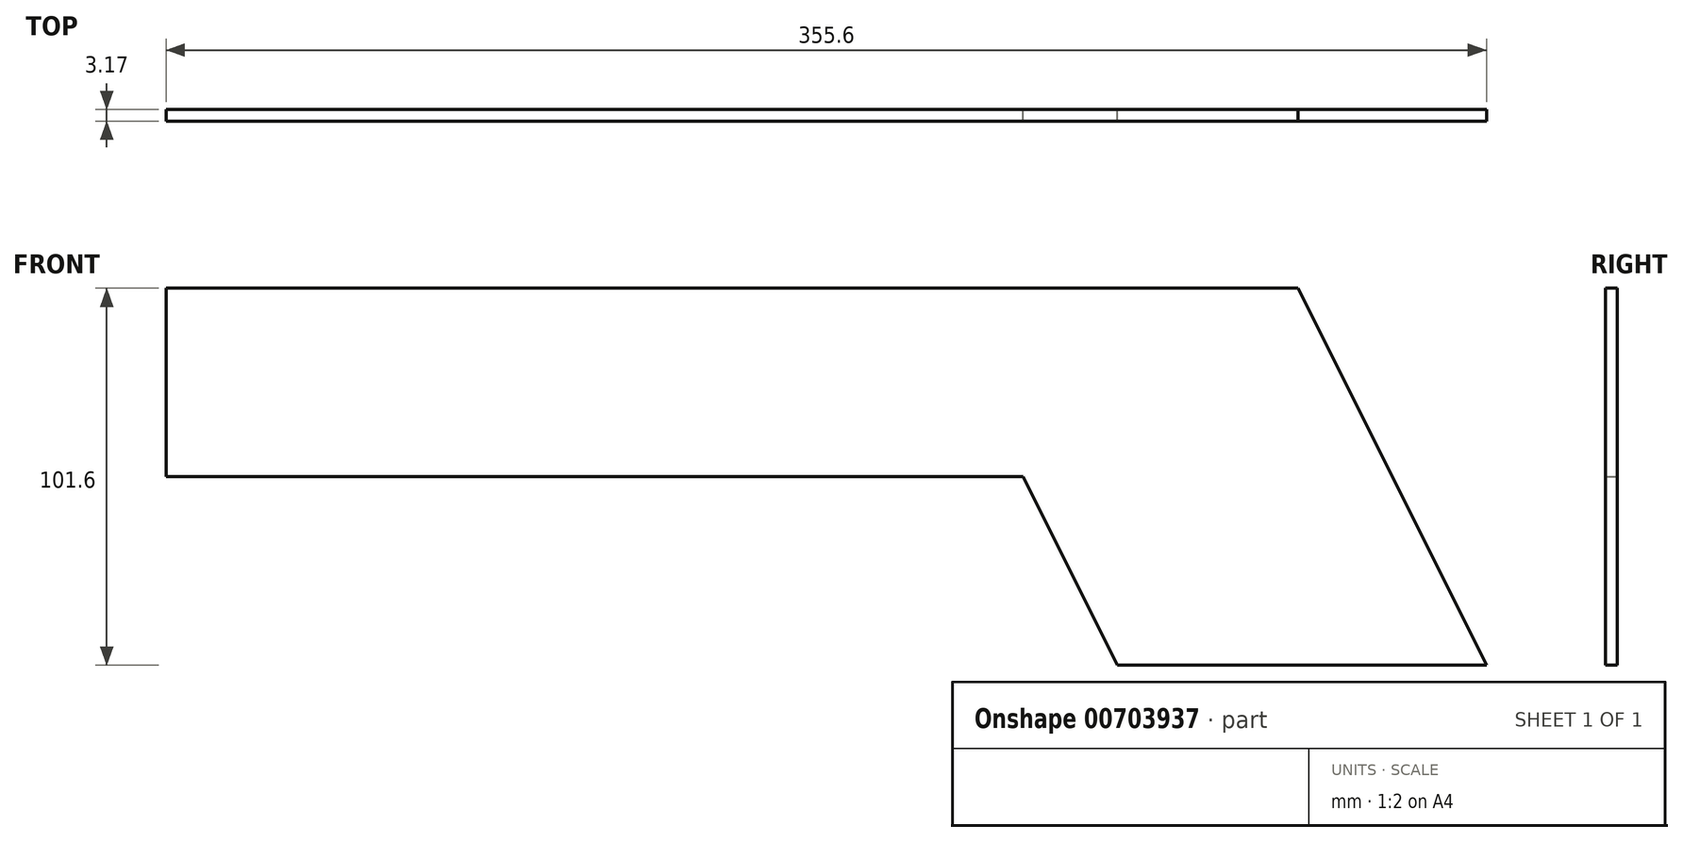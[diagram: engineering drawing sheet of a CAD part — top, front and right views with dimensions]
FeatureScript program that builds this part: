
annotation { "Feature Type Name" : "Feature", "Feature Type Description" : "" }
export const myFeature = defineFeature(function(context is Context, id is Id, definition is map)
    precondition{}
    {
        {
            var Q0;
            Q0=qCreatedBy(makeId("Front.planeOp"),FACE);
            var sketch = newSketch(context, id + "F0", { "sketchPlane" : qUnion([Q0])});
            skLineSegment(sketch, "E0", {"start": v(0, 0) * mm, "end": v(0, -50.8) * mm});
            skLineSegment(sketch, "E1", {"start": v(-256.2, -101.6) * mm, "end": v(-355.6, -101.6) * mm});
            skLineSegment(sketch, "E2", {"start": v(-355.6, -101.6) * mm, "end": v(-256.2, -101.6) * mm});
            skLineSegment(sketch, "E3", {"start": v(-304.8, 0) * mm, "end": v(-355.6, -101.6) * mm});
            skLineSegment(sketch, "E4", {"start": v(304.8, 0) * mm, "end": v(355.6, -101.6) * mm});
            skLineSegment(sketch, "E5", {"start": v(406.4, 304.8) * mm, "end": v(304.8, 0) * mm});
            skLineSegment(sketch, "E6", {"start": v(-389.47, 254) * mm, "end": v(-406.4, 304.8) * mm});
            skLineSegment(sketch, "E7", {"start": v(-318.99, 203.2) * mm, "end": v(-306.29, 165.1) * mm});
            skLineSegment(sketch, "E8", {"start": v(-166.59, 50.8) * mm, "end": v(268.19, 50.8) * mm});
            skLineSegment(sketch, "E9", {"start": v(335.92, 254) * mm, "end": v(-335.92, 254) * mm});
            skLineSegment(sketch, "E10", {"start": v(335.92, 254) * mm, "end": v(268.19, 50.8) * mm});
            skLineSegment(sketch, "E11", {"start": v(-256.2, -101.6) * mm, "end": v(-230.8, -50.8) * mm});
            skLineSegment(sketch, "E12", {"start": v(-230.8, -50.8) * mm, "end": v(230.8, -50.8) * mm});
            skLineSegment(sketch, "E13", {"start": v(230.8, -50.8) * mm, "end": v(256.2, -101.6) * mm});
            skLineSegment(sketch, "E14.trimOffspring", {"start": v(256.2, -101.6) * mm, "end": v(355.6, -101.6) * mm});
            skPoint(sketch, "E15.orphan", {"position": v(0, -101.6) * mm});
            skPoint(sketch, "E16", {"position": v(-215.9, 0) * mm});
            skPoint(sketch, "E17", {"position": v(-88.9, 0) * mm});
            skPoint(sketch, "E18", {"position": v(88.9, 0) * mm});
            skPoint(sketch, "E19", {"position": v(215.9, 0) * mm});
            skLineSegment(sketch, "E20", {"start": v(-217.39, 50.8) * mm, "end": v(-242.79, 76.2) * mm});
            skPoint(sketch, "E21.end.orphan", {"position": v(-391.2, 0) * mm});
            skLineSegment(sketch, "E22.1.0.0", {"start": v(-191.99, 76.2) * mm, "end": v(-217.39, 101.6) * mm});
            skLineSegment(sketch, "E22.2.0.0", {"start": v(-115.79, 50.8) * mm, "end": v(-141.19, 76.2) * mm});
            skLineSegment(sketch, "E22.3.0.0", {"start": v(-90.39, 76.2) * mm, "end": v(-115.79, 101.6) * mm});
            skLineSegment(sketch, "E22.4.0.0", {"start": v(-14.19, 50.8) * mm, "end": v(-39.59, 76.2) * mm});
            skLineSegment(sketch, "E22.5.0.0", {"start": v(11.21, 76.2) * mm, "end": v(-14.19, 101.6) * mm});
            skLineSegment(sketch, "E22.6.0.0", {"start": v(87.41, 50.8) * mm, "end": v(62.01, 76.2) * mm});
            skLineSegment(sketch, "E22.7.0.0", {"start": v(112.81, 76.2) * mm, "end": v(87.41, 101.6) * mm});
            skLineSegment(sketch, "E22.8.0.0", {"start": v(189.01, 50.8) * mm, "end": v(163.61, 76.2) * mm});
            skLineSegment(sketch, "E22.9.0.0", {"start": v(214.41, 76.2) * mm, "end": v(189.01, 101.6) * mm});
            skLineSegment(sketch, "E22.10.0.0", {"start": v(273.8, 67.62) * mm, "end": v(265.21, 76.2) * mm});
            skLineSegment(sketch, "E22.12.0.0", {"start": v(290.61, 152.4) * mm, "end": v(265.21, 177.8) * mm});
            skLineSegment(sketch, "E22.14.0.0", {"start": v(324.6, 220.02) * mm, "end": v(316.01, 228.6) * mm});
            skLineSegment(sketch, "E22.direction1", {"start": v(-420.59, 254) * mm, "end": v(-369.79, 254) * mm, "construction": true});
            skLineSegment(sketch, "E23.3.0.0", {"start": v(-166.59, 254) * mm, "end": v(-191.99, 228.6) * mm});
            skLineSegment(sketch, "E23.4.0.0", {"start": v(-141.19, 228.6) * mm, "end": v(-166.59, 203.2) * mm});
            skLineSegment(sketch, "E23.5.0.0", {"start": v(-64.99, 254) * mm, "end": v(-90.39, 228.6) * mm});
            skLineSegment(sketch, "E23.6.0.0", {"start": v(-39.59, 228.6) * mm, "end": v(-64.99, 203.2) * mm});
            skLineSegment(sketch, "E23.7.0.0", {"start": v(36.61, 254) * mm, "end": v(11.21, 228.6) * mm});
            skLineSegment(sketch, "E23.8.0.0", {"start": v(62.01, 228.6) * mm, "end": v(36.61, 203.2) * mm});
            skLineSegment(sketch, "E23.9.0.0", {"start": v(138.21, 254) * mm, "end": v(112.81, 228.6) * mm});
            skLineSegment(sketch, "E23.10.0.0", {"start": v(163.61, 228.6) * mm, "end": v(138.21, 203.2) * mm});
            skLineSegment(sketch, "E23.11.0.0", {"start": v(239.81, 254) * mm, "end": v(214.41, 228.6) * mm});
            skLineSegment(sketch, "E23.12.0.0", {"start": v(265.21, 228.6) * mm, "end": v(239.81, 203.2) * mm});
            skLineSegment(sketch, "E23.13.0.0", {"start": v(333.17, 245.76) * mm, "end": v(316.01, 228.6) * mm});
            skPoint(sketch, "E24.orphan", {"position": v(-420.59, 50.8) * mm});
            skPoint(sketch, "E25.orphan", {"position": v(-369.79, 50.8) * mm});
            skPoint(sketch, "E26.orphan", {"position": v(-318.99, 50.8) * mm});
            skPoint(sketch, "E27.orphan", {"position": v(290.61, 50.8) * mm});
            skLineSegment(sketch, "E28.trimOffspring", {"start": v(265.21, 127) * mm, "end": v(239.81, 152.4) * mm});
            skPoint(sketch, "E29.orphan", {"position": v(392.21, 50.8) * mm});
            skLineSegment(sketch, "E30.trimOffspring", {"start": v(311.9, 181.92) * mm, "end": v(290.61, 203.2) * mm});
            skPoint(sketch, "E31.orphan", {"position": v(493.81, 50.8) * mm});
            skLineSegment(sketch, "E32.trimOffspring", {"start": v(307.77, 169.56) * mm, "end": v(290.61, 152.4) * mm});
            skPoint(sketch, "E33.orphan", {"position": v(341.41, 254) * mm});
            skPoint(sketch, "E23.direction1.start.orphan", {"position": v(-522.19, 50.8) * mm});
            skLineSegment(sketch, "E34.trimOffspring", {"start": v(-268.19, 203.2) * mm, "end": v(-293.59, 228.6) * mm});
            skLineSegment(sketch, "E35.trimOffspring", {"start": v(-293.59, 177.8) * mm, "end": v(-318.99, 203.2) * mm});
            skLineSegment(sketch, "E36.trimOffspring", {"start": v(-268.19, 152.4) * mm, "end": v(-293.59, 127) * mm});
            skLineSegment(sketch, "E37.trimOffspring", {"start": v(-217.39, 203.2) * mm, "end": v(-242.79, 177.8) * mm});
            skLineSegment(sketch, "E38.trimOffspring", {"start": v(-242.79, 127) * mm, "end": v(-268.19, 101.6) * mm});
            skLineSegment(sketch, "E39.trimOffspring", {"start": v(-268.19, 101.6) * mm, "end": v(-293.59, 127) * mm});
            skLineSegment(sketch, "E40.trimOffspring", {"start": v(-242.79, 127) * mm, "end": v(-268.19, 152.4) * mm});
            skPoint(sketch, "E41.orphan", {"position": v(-166.59, 50.8) * mm});
            skLineSegment(sketch, "E42.trimOffspring", {"start": v(-166.59, 101.6) * mm, "end": v(-191.99, 127) * mm});
            skLineSegment(sketch, "E43.trimOffspring", {"start": v(-217.39, 152.4) * mm, "end": v(-242.79, 177.8) * mm});
            skLineSegment(sketch, "E44.trimOffspring", {"start": v(-191.99, 76.2) * mm, "end": v(-217.39, 50.8) * mm});
            skLineSegment(sketch, "E45.trimOffspring", {"start": v(-141.19, 127) * mm, "end": v(-166.59, 152.4) * mm});
            skLineSegment(sketch, "E46.trimOffspring", {"start": v(-166.59, 152.4) * mm, "end": v(-191.99, 127) * mm});
            skLineSegment(sketch, "E47.trimOffspring", {"start": v(-191.99, 177.8) * mm, "end": v(-217.39, 203.2) * mm});
            skLineSegment(sketch, "E48.trimOffspring", {"start": v(-191.99, 177.8) * mm, "end": v(-217.39, 152.4) * mm});
            skLineSegment(sketch, "E49.trimOffspring", {"start": v(-242.79, 228.6) * mm, "end": v(-268.19, 254) * mm});
            skPoint(sketch, "E50.orphan", {"position": v(-217.39, 254) * mm});
            skLineSegment(sketch, "E51.trimOffspring", {"start": v(-166.59, 203.2) * mm, "end": v(-191.99, 228.6) * mm});
            skLineSegment(sketch, "E52.trimOffspring", {"start": v(-141.19, 228.6) * mm, "end": v(-166.59, 254) * mm});
            skLineSegment(sketch, "E53.trimOffspring", {"start": v(-115.79, 203.2) * mm, "end": v(-141.19, 177.8) * mm});
            skLineSegment(sketch, "E54.trimOffspring", {"start": v(-90.39, 177.8) * mm, "end": v(-115.79, 152.4) * mm});
            skLineSegment(sketch, "E55.trimOffspring", {"start": v(-90.39, 177.8) * mm, "end": v(-115.79, 203.2) * mm});
            skLineSegment(sketch, "E56.trimOffspring", {"start": v(-115.79, 152.4) * mm, "end": v(-141.19, 177.8) * mm});
            skLineSegment(sketch, "E57.trimOffspring", {"start": v(-115.79, 101.6) * mm, "end": v(-141.19, 76.2) * mm});
            skLineSegment(sketch, "E58.trimOffspring", {"start": v(-90.39, 76.2) * mm, "end": v(-115.79, 50.8) * mm});
            skPoint(sketch, "E59.orphan", {"position": v(-64.99, 50.8) * mm});
            skLineSegment(sketch, "E60.trimOffspring", {"start": v(-64.99, 101.6) * mm, "end": v(-90.39, 127) * mm});
            skLineSegment(sketch, "E61.trimOffspring", {"start": v(-39.59, 127) * mm, "end": v(-64.99, 152.4) * mm});
            skLineSegment(sketch, "E62.trimOffspring", {"start": v(-39.59, 127) * mm, "end": v(-64.99, 101.6) * mm});
            skLineSegment(sketch, "E63.trimOffspring", {"start": v(-64.99, 152.4) * mm, "end": v(-90.39, 127) * mm});
            skPoint(sketch, "E64.orphan", {"position": v(-115.79, 254) * mm});
            skLineSegment(sketch, "E65.trimOffspring", {"start": v(-64.99, 203.2) * mm, "end": v(-90.39, 228.6) * mm});
            skLineSegment(sketch, "E66.trimOffspring", {"start": v(-39.59, 228.6) * mm, "end": v(-64.99, 254) * mm});
            skLineSegment(sketch, "E67.trimOffspring", {"start": v(-14.19, 101.6) * mm, "end": v(-39.59, 76.2) * mm});
            skLineSegment(sketch, "E68.trimOffspring", {"start": v(-14.19, 203.2) * mm, "end": v(-39.59, 177.8) * mm});
            skLineSegment(sketch, "E69.trimOffspring", {"start": v(11.21, 177.8) * mm, "end": v(-14.19, 152.4) * mm});
            skLineSegment(sketch, "E70.trimOffspring", {"start": v(11.21, 177.8) * mm, "end": v(-14.19, 203.2) * mm});
            skLineSegment(sketch, "E71.trimOffspring", {"start": v(-14.19, 152.4) * mm, "end": v(-39.59, 177.8) * mm});
            skLineSegment(sketch, "E72.trimOffspring", {"start": v(11.21, 76.2) * mm, "end": v(-14.19, 50.8) * mm});
            skPoint(sketch, "E73.orphan", {"position": v(36.61, 50.8) * mm});
            skLineSegment(sketch, "E74.trimOffspring", {"start": v(36.61, 101.6) * mm, "end": v(11.21, 127) * mm});
            skPoint(sketch, "E75.orphan", {"position": v(-14.19, 254) * mm});
            skLineSegment(sketch, "E76.trimOffspring", {"start": v(36.61, 203.2) * mm, "end": v(11.21, 228.6) * mm});
            skLineSegment(sketch, "E77.trimOffspring", {"start": v(62.01, 228.6) * mm, "end": v(36.61, 254) * mm});
            skLineSegment(sketch, "E78.trimOffspring", {"start": v(36.61, 152.4) * mm, "end": v(11.21, 127) * mm});
            skPoint(sketch, "E79.orphan", {"position": v(87.41, 254) * mm});
            skLineSegment(sketch, "E80.trimOffspring", {"start": v(62.01, 127) * mm, "end": v(36.61, 101.6) * mm});
            skLineSegment(sketch, "E81.trimOffspring", {"start": v(112.81, 177.8) * mm, "end": v(87.41, 152.4) * mm});
            skLineSegment(sketch, "E82.trimOffspring", {"start": v(87.41, 203.2) * mm, "end": v(62.01, 177.8) * mm});
            skLineSegment(sketch, "E83.trimOffspring", {"start": v(62.01, 127) * mm, "end": v(36.61, 152.4) * mm});
            skLineSegment(sketch, "E84.trimOffspring", {"start": v(87.41, 101.6) * mm, "end": v(62.01, 76.2) * mm});
            skLineSegment(sketch, "E85.trimOffspring", {"start": v(87.41, 152.4) * mm, "end": v(62.01, 177.8) * mm});
            skLineSegment(sketch, "E86.trimOffspring", {"start": v(112.81, 177.8) * mm, "end": v(87.41, 203.2) * mm});
            skPoint(sketch, "E87.orphan", {"position": v(138.21, 50.8) * mm});
            skLineSegment(sketch, "E88.trimOffspring", {"start": v(112.81, 76.2) * mm, "end": v(87.41, 50.8) * mm});
            skLineSegment(sketch, "E89.trimOffspring", {"start": v(138.21, 101.6) * mm, "end": v(112.81, 127) * mm});
            skLineSegment(sketch, "E90.trimOffspring", {"start": v(163.61, 127) * mm, "end": v(138.21, 152.4) * mm});
            skLineSegment(sketch, "E91.trimOffspring", {"start": v(138.21, 152.4) * mm, "end": v(112.81, 127) * mm});
            skLineSegment(sketch, "E92.trimOffspring", {"start": v(163.61, 127) * mm, "end": v(138.21, 101.6) * mm});
            skLineSegment(sketch, "E93.trimOffspring", {"start": v(189.01, 101.6) * mm, "end": v(163.61, 76.2) * mm});
            skLineSegment(sketch, "E94.trimOffspring", {"start": v(138.21, 203.2) * mm, "end": v(112.81, 228.6) * mm});
            skLineSegment(sketch, "E95.trimOffspring", {"start": v(163.61, 228.6) * mm, "end": v(138.21, 254) * mm});
            skLineSegment(sketch, "E96.trimOffspring", {"start": v(189.01, 203.2) * mm, "end": v(163.61, 177.8) * mm});
            skLineSegment(sketch, "E97.trimOffspring", {"start": v(214.41, 177.8) * mm, "end": v(189.01, 152.4) * mm});
            skLineSegment(sketch, "E98.trimOffspring", {"start": v(214.41, 177.8) * mm, "end": v(189.01, 203.2) * mm});
            skLineSegment(sketch, "E99.trimOffspring", {"start": v(189.01, 152.4) * mm, "end": v(163.61, 177.8) * mm});
            skLineSegment(sketch, "E100.trimOffspring", {"start": v(214.41, 76.2) * mm, "end": v(189.01, 50.8) * mm});
            skPoint(sketch, "E101.orphan", {"position": v(239.81, 50.8) * mm});
            skPoint(sketch, "E102.orphan", {"position": v(189.01, 254) * mm});
            skLineSegment(sketch, "E103.trimOffspring", {"start": v(239.81, 203.2) * mm, "end": v(214.41, 228.6) * mm});
            skLineSegment(sketch, "E104.trimOffspring", {"start": v(239.81, 152.4) * mm, "end": v(214.41, 127) * mm});
            skLineSegment(sketch, "E105.trimOffspring", {"start": v(265.21, 127) * mm, "end": v(239.81, 101.6) * mm});
            skLineSegment(sketch, "E106.trimOffspring", {"start": v(265.21, 228.6) * mm, "end": v(239.81, 254) * mm});
            skPoint(sketch, "E107.orphan", {"position": v(290.61, 254) * mm});
            skLineSegment(sketch, "E108.trimOffspring", {"start": v(290.61, 203.2) * mm, "end": v(265.21, 177.8) * mm});
            skLineSegment(sketch, "E109", {"start": v(265.21, 76.2) * mm, "end": v(282.37, 93.36) * mm});
            skLineSegment(sketch, "E110.trimOffspring", {"start": v(239.81, 101.6) * mm, "end": v(214.41, 127) * mm});
            skLineSegment(sketch, "E111", {"start": v(-268.19, 203.2) * mm, "end": v(-242.79, 228.6) * mm});
            skLineSegment(sketch, "E112", {"start": v(-293.59, 228.6) * mm, "end": v(-268.19, 254) * mm});
            skLineSegment(sketch, "E113", {"start": v(-293.59, 177.8) * mm, "end": v(-306.29, 165.1) * mm});
            skPoint(sketch, "E113.endSnap0", {"position": v(-306.29, 190.5) * mm});
            skPoint(sketch, "E114.start.orphan", {"position": v(0, 304.8) * mm});
            skLineSegment(sketch, "E115", {"start": v(-304.8, 0) * mm, "end": v(304.8, 0) * mm});
            skLineSegment(sketch, "E116.trimOffspring", {"start": v(-293.59, 127) * mm, "end": v(-268.19, 50.8) * mm});
            skSolve(sketch);
        }
        {
            var Q0;
            Q0=makeQuery(id+"F0.imprint","IMPRINT",FACE,{"disambiguationData":[TD([[makeQuery(id+"F0.imprint","IMPRINT",EDGE,{"derivedFrom":sQuery(id+"F0.wireOp",EDGE,"E2")}),1.0]])]});
            var Q1;
            {var subQ1=sQuery(id+"F0.wireOp",EDGE,"E0");Q1=makeQuery(id+"F0.imprint","IMPRINT",FACE,{"disambiguationData":[TD([[makeQuery(id+"F0.imprint","IMPRINT",EDGE,{"derivedFrom":subQ1}),1.0]])]});}
            extrude(context, id + "F1", {"entities" : qUnion([Q0, Q1]), "depth" : 3.17 * mm, "offsetDistance" : 25.4 * mm});
        }
    });
